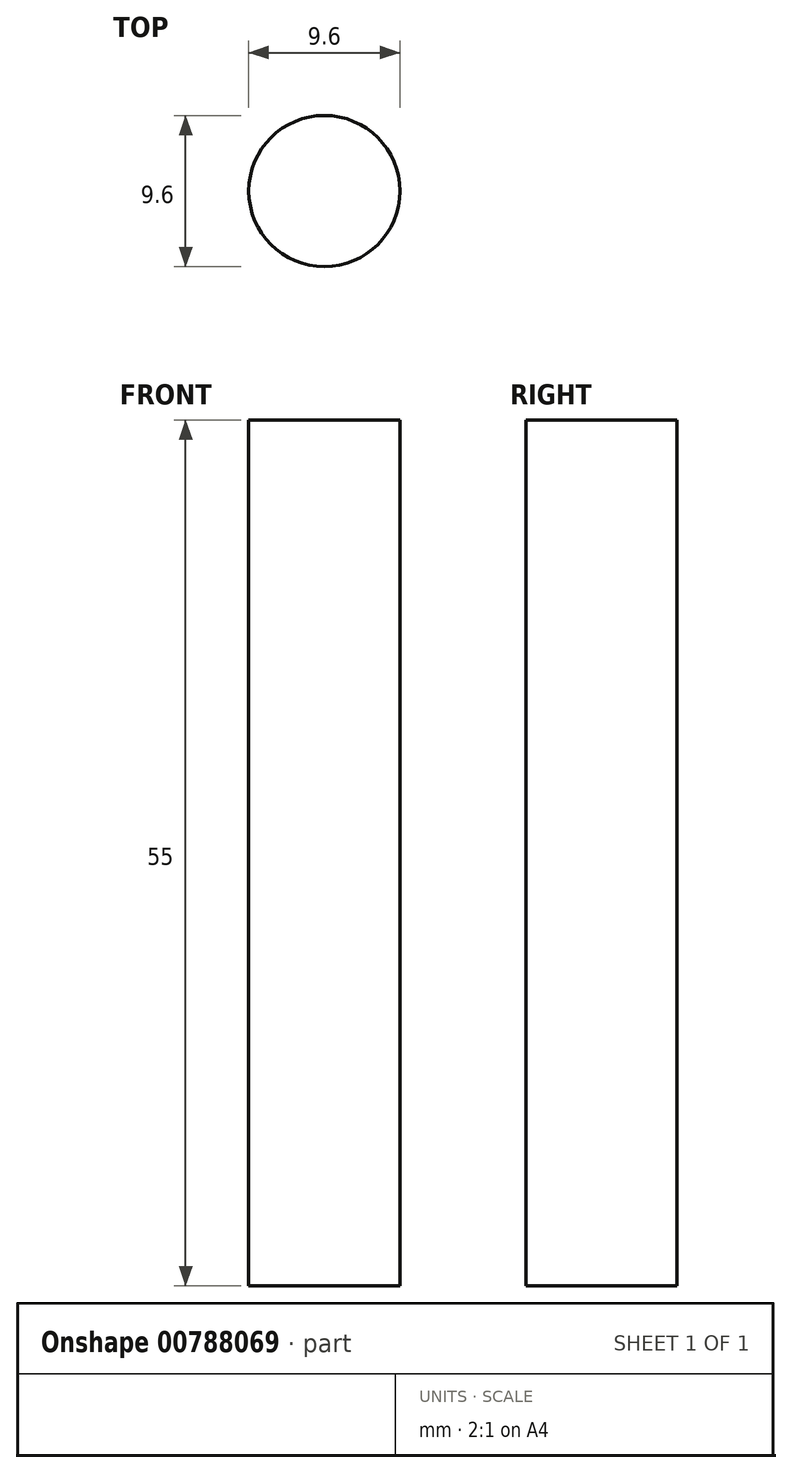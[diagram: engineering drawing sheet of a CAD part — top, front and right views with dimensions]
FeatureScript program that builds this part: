
annotation { "Feature Type Name" : "Feature", "Feature Type Description" : "" }
export const myFeature = defineFeature(function(context is Context, id is Id, definition is map)
    precondition{}
    {
        {
            var Q0;
            Q0=qCreatedBy(makeId("Top.planeOp"),FACE);
            var sketch = newSketch(context, id + "F0", { "sketchPlane" : qUnion([Q0])});
            skCircle(sketch, "E0", {"center": v(0, 0) * mm, "radius": 4.8 * mm});
            skSolve(sketch);
        }
        {
            var Q0;
            Q0=makeQuery(id+"F0.imprint","IMPRINT",FACE,{"disambiguationData":[TD([[makeQuery(id+"F0.imprint","IMPRINT",EDGE,{"derivedFrom":sQuery(id+"F0.wireOp",EDGE,"E0")}),1.0]])]});
            extrude(context, id + "F1", {"entities" : qUnion([Q0]), "depth" : 55 * mm, "offsetDistance" : 25 * mm});
        }
    });
